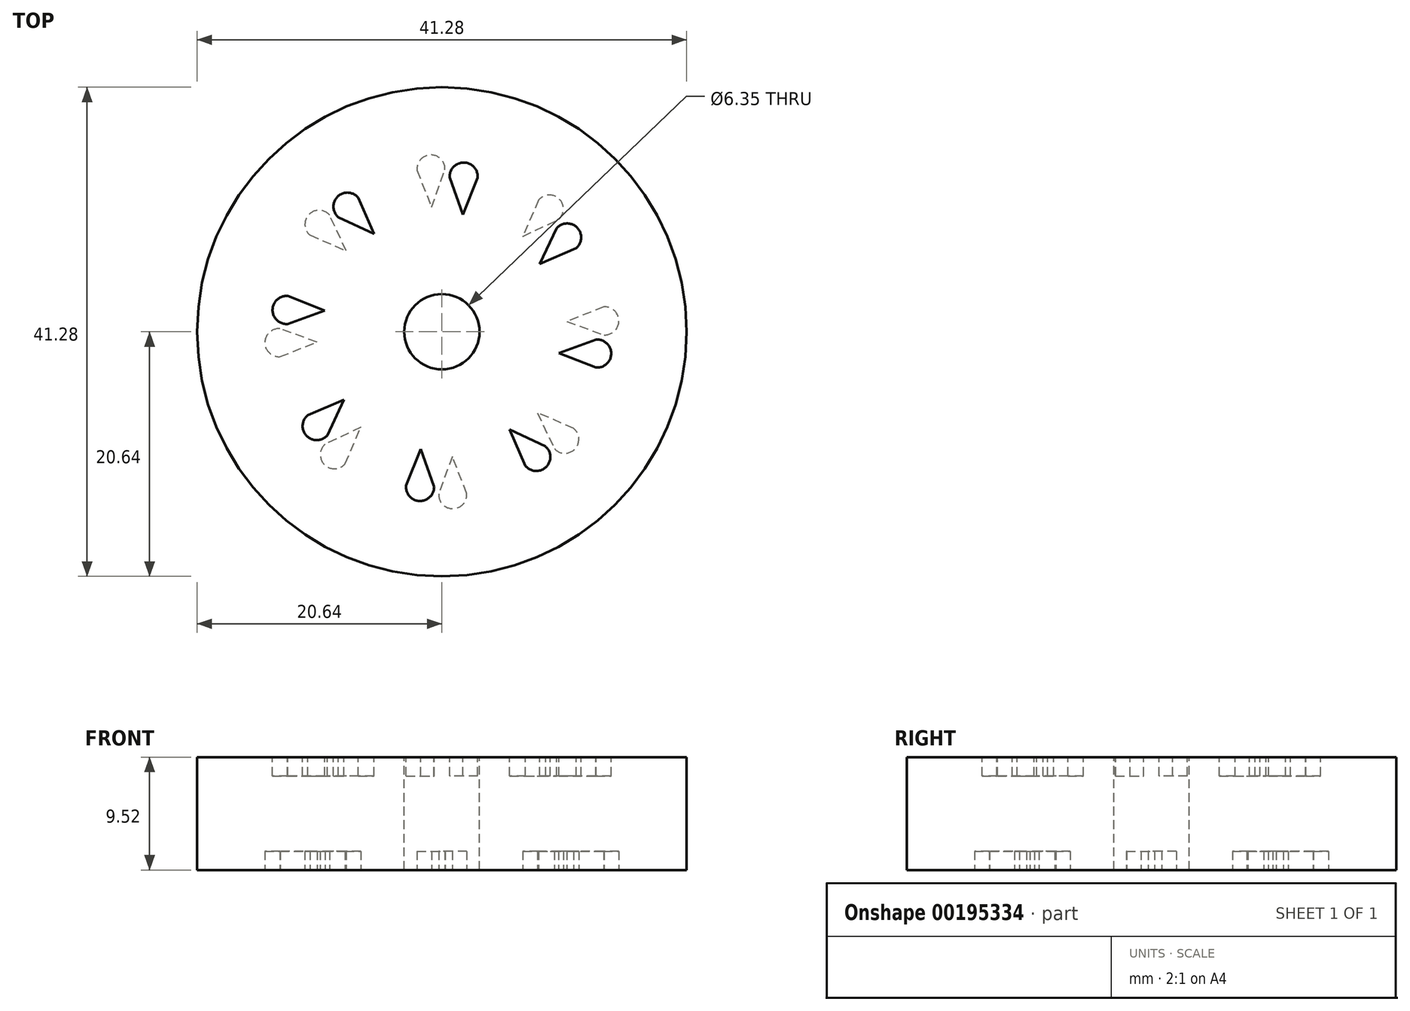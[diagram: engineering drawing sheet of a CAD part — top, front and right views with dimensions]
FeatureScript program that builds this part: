
annotation { "Feature Type Name" : "Feature", "Feature Type Description" : "" }
export const myFeature = defineFeature(function(context is Context, id is Id, definition is map)
    precondition{}
    {
        {
            var Q0;
            Q0=qCreatedBy(makeId("Top.planeOp"),FACE);
            var sketch = newSketch(context, id + "F0", { "sketchPlane" : qUnion([Q0])});
            skCircle(sketch, "E0", {"center": v(0, 0) * mm, "radius": 20.64 * mm});
            skSolve(sketch);
        }
        {
            var Q0;
            Q0 = qSketchRegion(id + "F0", true);
            extrude(context, id + "F1", {"entities" : qUnion([Q0]), "endBound" : BoundingType.SYMMETRIC, "depth" : 9.52 * mm});
        }
        {
            var Q0;
            Q0=qCreatedBy(makeId("Top.planeOp"),FACE);
            var sketch = newSketch(context, id + "F2", { "sketchPlane" : qUnion([Q0])});
            skCircle(sketch, "E1", {"center": v(0, 0) * mm, "radius": 3.18 * mm});
            skSolve(sketch);
        }
        {
            var Q0;
            Q0=makeQuery(id+"F1.opExtrude","CAP_FACE",FACE,{"disambiguationData":[OSD([sQuery(id+"F0.wireOp",EDGE,"E0")])],"isStart":false});
            var sketch = newSketch(context, id + "F3", { "sketchPlane" : qUnion([Q0])});
            skArc(sketch, "E2", {"start": v(-7.05, 11.31) * mm, "mid": v(-8.78, 11.4) * mm, "end": v(-8.74, 9.67) * mm});
            skLineSegment(sketch, "E3", {"start": v(-7.05, 11.31) * mm, "end": v(-5.72, 8.25) * mm});
            skLineSegment(sketch, "E4", {"start": v(-5.72, 8.25) * mm, "end": v(-8.74, 9.67) * mm});
            skArc(sketch, "E5.1.0", {"start": v(-12.99, 3.02) * mm, "mid": v(-14.28, 1.86) * mm, "end": v(-13.02, 0.66) * mm});
            skLineSegment(sketch, "E5.1.1", {"start": v(-12.99, 3.02) * mm, "end": v(-9.88, 1.79) * mm});
            skLineSegment(sketch, "E5.1.2", {"start": v(-9.88, 1.79) * mm, "end": v(-13.02, 0.66) * mm});
            skArc(sketch, "E5.2.0", {"start": v(-11.31, -7.05) * mm, "mid": v(-11.4, -8.78) * mm, "end": v(-9.67, -8.74) * mm});
            skLineSegment(sketch, "E5.2.1", {"start": v(-11.31, -7.05) * mm, "end": v(-8.25, -5.72) * mm});
            skLineSegment(sketch, "E5.2.2", {"start": v(-8.25, -5.72) * mm, "end": v(-9.67, -8.74) * mm});
            skArc(sketch, "E5.3.0", {"start": v(-3.02, -12.99) * mm, "mid": v(-1.86, -14.28) * mm, "end": v(-0.66, -13.02) * mm});
            skLineSegment(sketch, "E5.3.1", {"start": v(-3.02, -12.99) * mm, "end": v(-1.79, -9.88) * mm});
            skLineSegment(sketch, "E5.3.2", {"start": v(-1.79, -9.88) * mm, "end": v(-0.66, -13.02) * mm});
            skArc(sketch, "E5.4.0", {"start": v(7.05, -11.31) * mm, "mid": v(8.78, -11.4) * mm, "end": v(8.74, -9.67) * mm});
            skLineSegment(sketch, "E5.4.1", {"start": v(7.05, -11.31) * mm, "end": v(5.72, -8.25) * mm});
            skLineSegment(sketch, "E5.4.2", {"start": v(5.72, -8.25) * mm, "end": v(8.74, -9.67) * mm});
            skArc(sketch, "E5.5.0", {"start": v(12.99, -3.02) * mm, "mid": v(14.28, -1.86) * mm, "end": v(13.02, -0.66) * mm});
            skLineSegment(sketch, "E5.5.1", {"start": v(12.99, -3.02) * mm, "end": v(9.88, -1.79) * mm});
            skLineSegment(sketch, "E5.5.2", {"start": v(9.88, -1.79) * mm, "end": v(13.02, -0.66) * mm});
            skArc(sketch, "E5.6.0", {"start": v(11.31, 7.05) * mm, "mid": v(11.4, 8.78) * mm, "end": v(9.67, 8.74) * mm});
            skLineSegment(sketch, "E5.6.1", {"start": v(11.31, 7.05) * mm, "end": v(8.25, 5.72) * mm});
            skLineSegment(sketch, "E5.6.2", {"start": v(8.25, 5.72) * mm, "end": v(9.67, 8.74) * mm});
            skArc(sketch, "E5.7.0", {"start": v(3.02, 12.99) * mm, "mid": v(1.86, 14.28) * mm, "end": v(0.66, 13.02) * mm});
            skLineSegment(sketch, "E5.7.1", {"start": v(3.02, 12.99) * mm, "end": v(1.79, 9.88) * mm});
            skLineSegment(sketch, "E5.7.2", {"start": v(1.79, 9.88) * mm, "end": v(0.66, 13.02) * mm});
            skPoint(sketch, "E5.center", {"position": v(0, 0) * mm});
            skSolve(sketch);
        }
        {
            var Q0;
            Q0 = qSketchRegion(id + "F2", true);
            extrude(context, id + "F4", {"entities" : qUnion([Q0]), "operationType" : NewBodyOperationType.REMOVE, "endBound" : BoundingType.SYMMETRIC, "oppositeDirection" : true, "depth" : 25.4 * mm});
        }
        {
            var Q0;
            Q0 = qSketchRegion(id + "F3", true);
            extrude(context, id + "F5", {"entities" : qUnion([Q0]), "operationType" : NewBodyOperationType.REMOVE, "oppositeDirection" : true, "depth" : 1.59 * mm});
        }
        {
            var Q0;
            Q0=makeQuery(id+"F1.opExtrude","CAP_FACE",FACE,{"disambiguationData":[OSD([sQuery(id+"F0.wireOp",EDGE,"E0")])],"isStart":true});
            var sketch = newSketch(context, id + "F6", { "sketchPlane" : qUnion([Q0])});
            skArc(sketch, "E6", {"start": v(-8.16, 11.12) * mm, "mid": v(-9.9, 11.22) * mm, "end": v(-9.85, 9.48) * mm});
            skLineSegment(sketch, "E7", {"start": v(-8.16, 11.12) * mm, "end": v(-6.83, 8.06) * mm});
            skLineSegment(sketch, "E8", {"start": v(-6.83, 8.06) * mm, "end": v(-9.85, 9.48) * mm});
            skArc(sketch, "E9.1.0", {"start": v(-13.63, 2.1) * mm, "mid": v(-14.92, 0.94) * mm, "end": v(-13.67, -0.26) * mm});
            skLineSegment(sketch, "E9.1.1", {"start": v(-13.63, 2.1) * mm, "end": v(-10.53, 0.87) * mm});
            skLineSegment(sketch, "E9.1.2", {"start": v(-10.53, 0.87) * mm, "end": v(-13.67, -0.26) * mm});
            skArc(sketch, "E9.2.0", {"start": v(-11.12, -8.16) * mm, "mid": v(-11.22, -9.9) * mm, "end": v(-9.48, -9.85) * mm});
            skLineSegment(sketch, "E9.2.1", {"start": v(-11.12, -8.16) * mm, "end": v(-8.06, -6.83) * mm});
            skLineSegment(sketch, "E9.2.2", {"start": v(-8.06, -6.83) * mm, "end": v(-9.48, -9.85) * mm});
            skArc(sketch, "E9.3.0", {"start": v(-2.1, -13.63) * mm, "mid": v(-0.94, -14.92) * mm, "end": v(0.26, -13.67) * mm});
            skLineSegment(sketch, "E9.3.1", {"start": v(-2.1, -13.63) * mm, "end": v(-0.87, -10.53) * mm});
            skLineSegment(sketch, "E9.3.2", {"start": v(-0.87, -10.53) * mm, "end": v(0.26, -13.67) * mm});
            skArc(sketch, "E9.4.0", {"start": v(8.16, -11.12) * mm, "mid": v(9.9, -11.22) * mm, "end": v(9.85, -9.48) * mm});
            skLineSegment(sketch, "E9.4.1", {"start": v(8.16, -11.12) * mm, "end": v(6.83, -8.06) * mm});
            skLineSegment(sketch, "E9.4.2", {"start": v(6.83, -8.06) * mm, "end": v(9.85, -9.48) * mm});
            skArc(sketch, "E9.5.0", {"start": v(13.63, -2.1) * mm, "mid": v(14.92, -0.94) * mm, "end": v(13.67, 0.26) * mm});
            skLineSegment(sketch, "E9.5.1", {"start": v(13.63, -2.1) * mm, "end": v(10.53, -0.87) * mm});
            skLineSegment(sketch, "E9.5.2", {"start": v(10.53, -0.87) * mm, "end": v(13.67, 0.26) * mm});
            skArc(sketch, "E9.6.0", {"start": v(11.12, 8.16) * mm, "mid": v(11.22, 9.9) * mm, "end": v(9.48, 9.85) * mm});
            skLineSegment(sketch, "E9.6.1", {"start": v(11.12, 8.16) * mm, "end": v(8.06, 6.83) * mm});
            skLineSegment(sketch, "E9.6.2", {"start": v(8.06, 6.83) * mm, "end": v(9.48, 9.85) * mm});
            skArc(sketch, "E9.7.0", {"start": v(2.1, 13.63) * mm, "mid": v(0.94, 14.92) * mm, "end": v(-0.26, 13.67) * mm});
            skLineSegment(sketch, "E9.7.1", {"start": v(2.1, 13.63) * mm, "end": v(0.87, 10.53) * mm});
            skLineSegment(sketch, "E9.7.2", {"start": v(0.87, 10.53) * mm, "end": v(-0.26, 13.67) * mm});
            skPoint(sketch, "E9.center", {"position": v(0, 0) * mm});
            skSolve(sketch);
        }
        {
            var Q0;
            Q0 = qSketchRegion(id + "F6", true);
            extrude(context, id + "F7", {"entities" : qUnion([Q0]), "operationType" : NewBodyOperationType.REMOVE, "oppositeDirection" : true, "depth" : 1.59 * mm});
        }
    });
